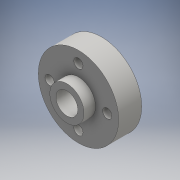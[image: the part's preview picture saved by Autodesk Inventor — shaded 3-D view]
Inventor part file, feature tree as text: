
AUTODESK INVENTOR PART (.ipt)
format: ipt  version: 2016 (Build 200138000, 138)  size: 134,656 bytes
history: native  units: mm
features: extrude x3, sketch x3
ambient origin geometry x8: Origin, YZ Plane, XZ Plane, XY Plane, X Axis, Y Axis, Z Axis, Center Point
bodies: Solid1 (feature_tree)
feature tree (6):
  extrude  "Extrusion1"  Depth=22.098mm
  extrude  "Extrusion2"  Depth=7.9375mm
  extrude  "Extrusion3"  Depth=6.35mm TaperAngle=0.0deg
  sketch  "Sketch1"  dims[d4=6.0mm d6=22.098mm]
  sketch  "Sketch2"  dims[d10=2.54mm d11=7.9375mm]
  sketch  "Sketch3"  dims[d12=40.0mm d14=360.0deg d16=6.35mm d17=0.0mm d18=6.0mm d19=9.398mm d20=3.175mm d21=0.0mm d22=6.0mm d23=9.398mm d24=3.175mm d25=0.0mm]
